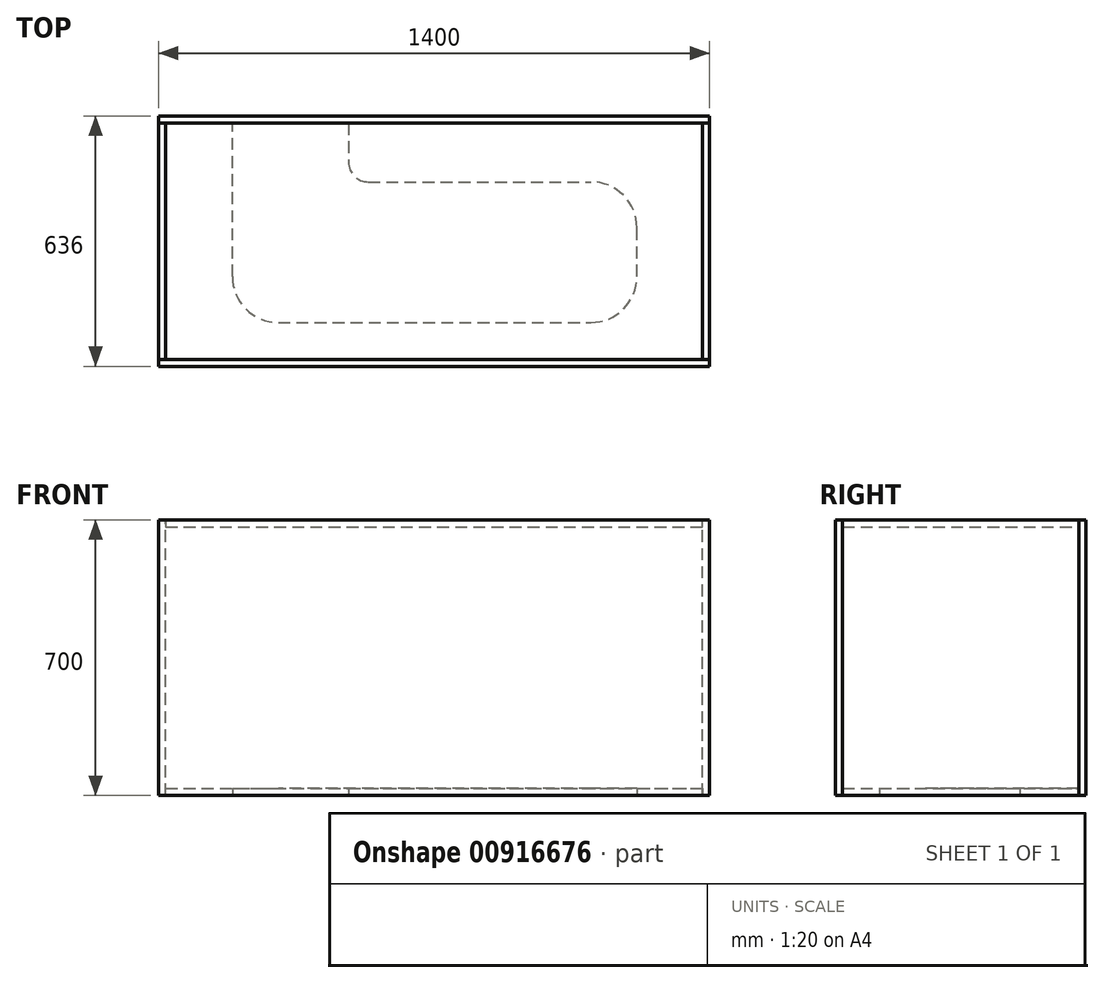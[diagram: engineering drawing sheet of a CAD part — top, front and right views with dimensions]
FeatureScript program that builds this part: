
annotation { "Feature Type Name" : "Feature", "Feature Type Description" : "" }
export const myFeature = defineFeature(function(context is Context, id is Id, definition is map)
    precondition{}
    {
        {
            var Q0;
            Q0=qCreatedBy(makeId("Front.planeOp"),FACE);
            var sketch = newSketch(context, id + "F0", { "sketchPlane" : qUnion([Q0])});
            skLineSegment(sketch, "E0.bottom", {"start": v(700, 350) * mm, "end": v(-700, 350) * mm});
            skLineSegment(sketch, "E0.top", {"start": v(700, -350) * mm, "end": v(-700, -350) * mm});
            skLineSegment(sketch, "E0.left", {"start": v(700, 350) * mm, "end": v(700, -350) * mm});
            skLineSegment(sketch, "E0.right", {"start": v(-700, 350) * mm, "end": v(-700, -350) * mm});
            skPoint(sketch, "E0.middle", {"position": v(0, 0) * mm});
            skSolve(sketch);
        }
        {
            var Q0;
            Q0=qCreatedBy(makeId("Front.planeOp"),FACE);
            var sketch = newSketch(context, id + "F1", { "sketchPlane" : qUnion([Q0])});
            skLineSegment(sketch, "E1.0.0", {"start": v(-700, -350) * mm, "end": v(-682, -350) * mm});
            skLineSegment(sketch, "E1.0.1", {"start": v(-682, -350) * mm, "end": v(-682, 350) * mm});
            skLineSegment(sketch, "E1.0.2", {"start": v(-682, 350) * mm, "end": v(-700, 350) * mm});
            skLineSegment(sketch, "E1.0.3", {"start": v(-700, 350) * mm, "end": v(-700, -350) * mm});
            skLineSegment(sketch, "E2.MirrorCS", {"start": v(700, 350) * mm, "end": v(700, -350) * mm});
            skLineSegment(sketch, "E3.MirrorCS", {"start": v(682, 350) * mm, "end": v(700, 350) * mm});
            skLineSegment(sketch, "E4.MirrorCS", {"start": v(682, -350) * mm, "end": v(682, 350) * mm});
            skLineSegment(sketch, "E5.MirrorCS", {"start": v(700, -350) * mm, "end": v(682, -350) * mm});
            skSolve(sketch);
        }
        {
            var Q0;
            Q0=makeQuery(id+"F0.imprint","IMPRINT",FACE,{"disambiguationData":[TD([[makeQuery(id+"F0.imprint","IMPRINT",EDGE,{"derivedFrom":sQuery(id+"F0.wireOp",EDGE,"E0.bottom")}),1.0]])]});
            extrude(context, id + "F2", {"entities" : qUnion([Q0]), "oppositeDirection" : true, "depth" : 18 * mm, "offsetDistance" : 25 * mm});
        }
        {
            var Q0;
            Q0 = qSketchRegion(id + "F1", true);
            extrude(context, id + "F3", {"entities" : qUnion([Q0]), "depth" : 600 * mm, "offsetDistance" : 25 * mm});
        }
        {
            var Q0;
            Q0=makeQuery(id+"F3.opExtrude","CAP_FACE",FACE,{"disambiguationData":[OSD([sQuery(id+"F1.wireOp",EDGE,"E1.0.0"),sQuery(id+"F1.wireOp",EDGE,"E1.0.1"),sQuery(id+"F1.wireOp",EDGE,"E1.0.2"),sQuery(id+"F1.wireOp",EDGE,"E1.0.3")])],"isStart":false});
            var sketch = newSketch(context, id + "F4", { "sketchPlane" : qUnion([Q0])});
            skLineSegment(sketch, "E6.0.0", {"start": v(-700, -350) * mm, "end": v(700, -350) * mm});
            skLineSegment(sketch, "E6.0.1", {"start": v(700, -350) * mm, "end": v(700, 350) * mm});
            skLineSegment(sketch, "E6.0.2", {"start": v(700, 350) * mm, "end": v(-700, 350) * mm});
            skLineSegment(sketch, "E6.0.3", {"start": v(-700, 350) * mm, "end": v(-700, -350) * mm});
            skSolve(sketch);
        }
        {
            var Q0;
            Q0=qCreatedBy(makeId("Front.planeOp"),FACE);
            var sketch = newSketch(context, id + "F5", { "sketchPlane" : qUnion([Q0])});
            skLineSegment(sketch, "E7.0.0", {"start": v(682, 332) * mm, "end": v(682, 350) * mm});
            skLineSegment(sketch, "E7.0.1", {"start": v(682, 350) * mm, "end": v(-682, 350) * mm});
            skLineSegment(sketch, "E7.0.2", {"start": v(-682, 350) * mm, "end": v(-682, 332) * mm});
            skLineSegment(sketch, "E7.0.3", {"start": v(-682, 332) * mm, "end": v(682, 332) * mm});
            skLineSegment(sketch, "E8.MirrorCS", {"start": v(-682, -332) * mm, "end": v(682, -332) * mm});
            skLineSegment(sketch, "E9.MirrorCS", {"start": v(682, -350) * mm, "end": v(-682, -350) * mm});
            skLineSegment(sketch, "E10.MirrorCS", {"start": v(-682, -350) * mm, "end": v(-682, -332) * mm});
            skLineSegment(sketch, "E11.MirrorCS", {"start": v(682, -332) * mm, "end": v(682, -350) * mm});
            skSolve(sketch);
        }
        {
            var Q0;
            Q0 = qSketchRegion(id + "F5", true);
            extrude(context, id + "F6", {"entities" : qUnion([Q0]), "depth" : 600 * mm, "offsetDistance" : 25 * mm});
        }
        {
            var Q0;
            Q0 = qSketchRegion(id + "F4", true);
            extrude(context, id + "F7", {"entities" : qUnion([Q0]), "depth" : 18 * mm, "offsetDistance" : 25 * mm});
        }
        {
            var Q0;
            Q0=makeQuery(id+"F6.opExtrude","SWEPT_FACE",FACE,{"disambiguationData":[OSD([sQuery(id+"F5.wireOp",EDGE,"E9.MirrorCS")])]});
            var sketch = newSketch(context, id + "F8", { "sketchPlane" : qUnion([Q0])});
            skLineSegment(sketch, "E12.bottom", {"start": v(-395.58, 506.22) * mm, "end": v(398.61, 506.22) * mm});
            skLineSegment(sketch, "E12.top", {"start": v(-167.2, 149.19) * mm, "end": v(398.61, 149.19) * mm});
            skLineSegment(sketch, "E12.left", {"start": v(-512.33, 389.47) * mm, "end": v(-512.33, 0) * mm});
            skLineSegment(sketch, "E12.right", {"start": v(515.36, 389.47) * mm, "end": v(515.36, 265.94) * mm});
            skLineSegment(sketch, "E13.bottom", {"start": v(-512.33, 0) * mm, "end": v(-217.2, 0) * mm});
            skLineSegment(sketch, "E13.right", {"start": v(-217.2, 0) * mm, "end": v(-217.2, 99.19) * mm});
            skPoint(sketch, "E14.visualSharp", {"position": v(-512.33, 506.22) * mm});
            skArc(sketch, "E14.filletArc", {"start": v(-395.58, 506.22) * mm, "mid": v(-478.13, 472.02) * mm, "end": v(-512.33, 389.47) * mm});
            skPoint(sketch, "E15.visualSharp", {"position": v(515.36, 506.22) * mm});
            skArc(sketch, "E15.filletArc", {"start": v(515.36, 389.47) * mm, "mid": v(481.17, 472.02) * mm, "end": v(398.61, 506.22) * mm});
            skPoint(sketch, "E16.visualSharp", {"position": v(515.36, 149.19) * mm});
            skArc(sketch, "E16.filletArc", {"start": v(398.61, 149.19) * mm, "mid": v(481.17, 183.38) * mm, "end": v(515.36, 265.94) * mm});
            skPoint(sketch, "E17.visualSharp", {"position": v(-217.2, 149.19) * mm});
            skArc(sketch, "E17.filletArc", {"start": v(-167.2, 149.19) * mm, "mid": v(-202.56, 134.54) * mm, "end": v(-217.2, 99.19) * mm});
            skSolve(sketch);
        }
        {
            var Q0;
            Q0=makeQuery(id+"F8.imprint","IMPRINT",FACE,{"disambiguationData":[TD([[makeQuery(id+"F8.imprint","IMPRINT",EDGE,{"derivedFrom":sQuery(id+"F8.wireOp",EDGE,"E12.bottom")}),-1.0]])]});
            extrude(context, id + "F9", {"entities" : qUnion([Q0]), "operationType" : NewBodyOperationType.REMOVE, "oppositeDirection" : true, "depth" : 25 * mm, "offsetDistance" : 25 * mm});
        }
    });
